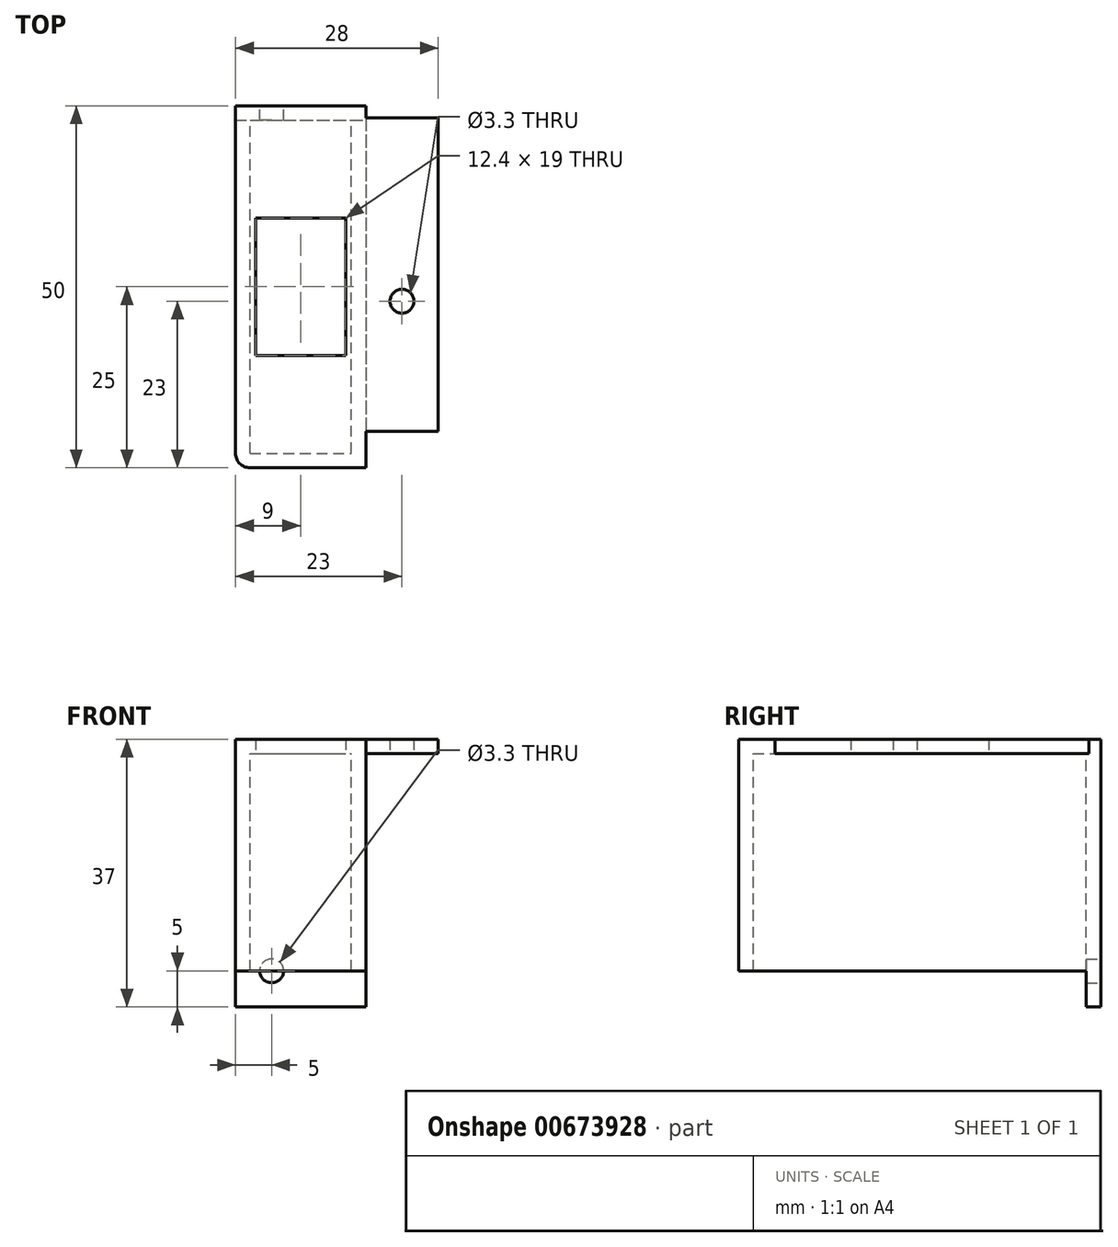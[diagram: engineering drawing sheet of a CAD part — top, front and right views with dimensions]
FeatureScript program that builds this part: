
annotation { "Feature Type Name" : "Feature", "Feature Type Description" : "" }
export const myFeature = defineFeature(function(context is Context, id is Id, definition is map)
    precondition{}
    {
        {
            var Q0;
            Q0=qCreatedBy(makeId("Top.planeOp"),FACE);
            var sketch = newSketch(context, id + "F0", { "sketchPlane" : qUnion([Q0])});
            skLineSegment(sketch, "E0.bottom", {"start": v(-9, 25) * mm, "end": v(9, 25) * mm});
            skLineSegment(sketch, "E0.top", {"start": v(-7, -25) * mm, "end": v(9, -25) * mm});
            skLineSegment(sketch, "E0.left", {"start": v(-9, 25) * mm, "end": v(-9, -23) * mm});
            skLineSegment(sketch, "E0.right", {"start": v(9, 25) * mm, "end": v(9, -25) * mm});
            skPoint(sketch, "E0.middle", {"position": v(0, 0) * mm});
            skLineSegment(sketch, "E1.bottom", {"start": v(-6.2, 9.5) * mm, "end": v(6.2, 9.5) * mm});
            skLineSegment(sketch, "E1.top", {"start": v(-6.2, -9.5) * mm, "end": v(6.2, -9.5) * mm});
            skLineSegment(sketch, "E1.left", {"start": v(-6.2, 9.5) * mm, "end": v(-6.2, -9.5) * mm});
            skLineSegment(sketch, "E1.right", {"start": v(6.2, 9.5) * mm, "end": v(6.2, -9.5) * mm});
            skLineSegment(sketch, "E2.bottom", {"start": v(9, 23.35) * mm, "end": v(19, 23.35) * mm});
            skLineSegment(sketch, "E2.top", {"start": v(9, -20) * mm, "end": v(19, -20) * mm});
            skLineSegment(sketch, "E2.left", {"start": v(9, 23.35) * mm, "end": v(9, -20) * mm});
            skLineSegment(sketch, "E2.right", {"start": v(19, 23.35) * mm, "end": v(19, -20) * mm});
            skCircle(sketch, "E3", {"center": v(14, -2) * mm, "radius": 1.65 * mm});
            skPoint(sketch, "E4.visualSharp", {"position": v(-9, -25) * mm});
            skArc(sketch, "E4.filletArc", {"start": v(-9, -23) * mm, "mid": v(-8.41, -24.41) * mm, "end": v(-7, -25) * mm});
            skLineSegment(sketch, "E5.bottom", {"start": v(-7, -23) * mm, "end": v(7, -23) * mm});
            skLineSegment(sketch, "E5.top", {"start": v(-7, 23) * mm, "end": v(7, 23) * mm});
            skLineSegment(sketch, "E5.left", {"start": v(-7, -23) * mm, "end": v(-7, 23) * mm});
            skLineSegment(sketch, "E5.right", {"start": v(7, -23) * mm, "end": v(7, 23) * mm});
            skSolve(sketch);
        }
        {
            var Q0;
            {var subQ3=sQuery(id+"F0.wireOp",EDGE,"E0.bottom");Q0=makeQuery(id+"F0.imprint","IMPRINT",FACE,{"disambiguationData":[TD([[makeQuery(id+"F0.imprint","IMPRINT",EDGE,{"derivedFrom":subQ3}),-1.0]])]});}
            var Q1;
            Q1=makeQuery(id+"F0.imprint","IMPRINT",FACE,{"disambiguationData":[TD([[makeQuery(id+"F0.imprint","IMPRINT",EDGE,{"derivedFrom":sQuery(id+"F0.wireOp",EDGE,"E2.bottom")}),-1.0]])]});
            var Q2;
            Q2=makeQuery(id+"F0.imprint","IMPRINT",FACE,{"disambiguationData":[TD([[makeQuery(id+"F0.imprint","IMPRINT",EDGE,{"derivedFrom":sQuery(id+"F0.wireOp",EDGE,"E1.bottom")}),1.0]])]});
            extrude(context, id + "F1", {"entities" : qUnion([Q0, Q1, Q2]), "depth" : 2 * mm, "offsetDistance" : 25 * mm});
        }
        {
            var Q0;
            {var subQ3=sQuery(id+"F0.wireOp",EDGE,"E0.bottom");Q0=makeQuery(id+"F0.imprint","IMPRINT",FACE,{"disambiguationData":[TD([[makeQuery(id+"F0.imprint","IMPRINT",EDGE,{"derivedFrom":subQ3}),-1.0]])]});}
            extrude(context, id + "F2", {"entities" : qUnion([Q0]), "operationType" : NewBodyOperationType.ADD, "oppositeDirection" : true, "depth" : 30 * mm, "offsetDistance" : 25 * mm});
        }
        {
            var Q0;
            Q0=makeQuery(id+"F2.opExtrude","CAP_FACE",FACE,{"disambiguationData":[OSD([sQuery(id+"F0.wireOp",EDGE,"E0.bottom"),sQuery(id+"F0.wireOp",EDGE,"E0.top"),sQuery(id+"F0.wireOp",EDGE,"E0.left"),sQuery(id+"F0.wireOp",EDGE,"E0.right"),sQuery(id+"F0.wireOp",EDGE,"E2.left"),sQuery(id+"F0.wireOp",EDGE,"E4.filletArc"),sQuery(id+"F0.wireOp",EDGE,"E5.bottom"),sQuery(id+"F0.wireOp",EDGE,"E5.top"),sQuery(id+"F0.wireOp",EDGE,"E5.left"),sQuery(id+"F0.wireOp",EDGE,"E5.right")])],"isStart":false});
            var sketch = newSketch(context, id + "F3", { "sketchPlane" : qUnion([Q0])});
            skLineSegment(sketch, "E6.bottom", {"start": v(-9, -25) * mm, "end": v(9, -25) * mm});
            skLineSegment(sketch, "E6.top", {"start": v(-9, -23) * mm, "end": v(9, -23) * mm});
            skLineSegment(sketch, "E6.left", {"start": v(-9, -25) * mm, "end": v(-9, -23) * mm});
            skLineSegment(sketch, "E6.right", {"start": v(9, -25) * mm, "end": v(9, -23) * mm});
            skSolve(sketch);
        }
        {
            var Q0;
            Q0=makeQuery(id+"F3.imprint","IMPRINT",FACE,{"disambiguationData":[TD([[makeQuery(id+"F3.imprint","IMPRINT",EDGE,{"derivedFrom":sQuery(id+"F3.wireOp",EDGE,"E6.bottom")}),1.0]])]});
            extrude(context, id + "F4", {"entities" : qUnion([Q0]), "operationType" : NewBodyOperationType.ADD, "depth" : 5 * mm, "offsetDistance" : 25 * mm});
        }
        {
            var Q0;
            {var subQ0=sQuery(id+"F0.wireOp",EDGE,"E0.bottom");Q0=makeQuery(id+"F4.boolean.opBoolean","MERGE",FACE,{"derivedFrom":[makeQuery(id+"F2.boolean.opBoolean","MERGE",FACE,{"derivedFrom":[makeQuery(id+"F1.opExtrude","SWEPT_FACE",FACE,{"disambiguationData":[OSD([subQ0])]}),makeQuery(id+"F2.opExtrude","SWEPT_FACE",FACE,{"disambiguationData":[OSD([subQ0])]})]}),makeQuery(id+"F4.opExtrude","SWEPT_FACE",FACE,{"disambiguationData":[OSD([sQuery(id+"F3.wireOp",EDGE,"E6.bottom")])]})]});}
            var sketch = newSketch(context, id + "F5", { "sketchPlane" : qUnion([Q0])});
            skCircle(sketch, "E7", {"center": v(4, -30) * mm, "radius": 1.65 * mm});
            skSolve(sketch);
        }
        {
            var Q0;
            Q0=makeQuery(id+"F5.imprint","IMPRINT",FACE,{"disambiguationData":[TD([[makeQuery(id+"F5.imprint","IMPRINT",EDGE,{"derivedFrom":sQuery(id+"F5.wireOp",EDGE,"E7")}),1.0]])]});
            extrude(context, id + "F6", {"entities" : qUnion([Q0]), "operationType" : NewBodyOperationType.REMOVE, "oppositeDirection" : true, "depth" : 25 * mm, "offsetDistance" : 25 * mm, "hasSecondDirection" : true, "secondDirectionOppositeDirection" : false, "secondDirectionDepth" : 25 * mm});
        }
    });
